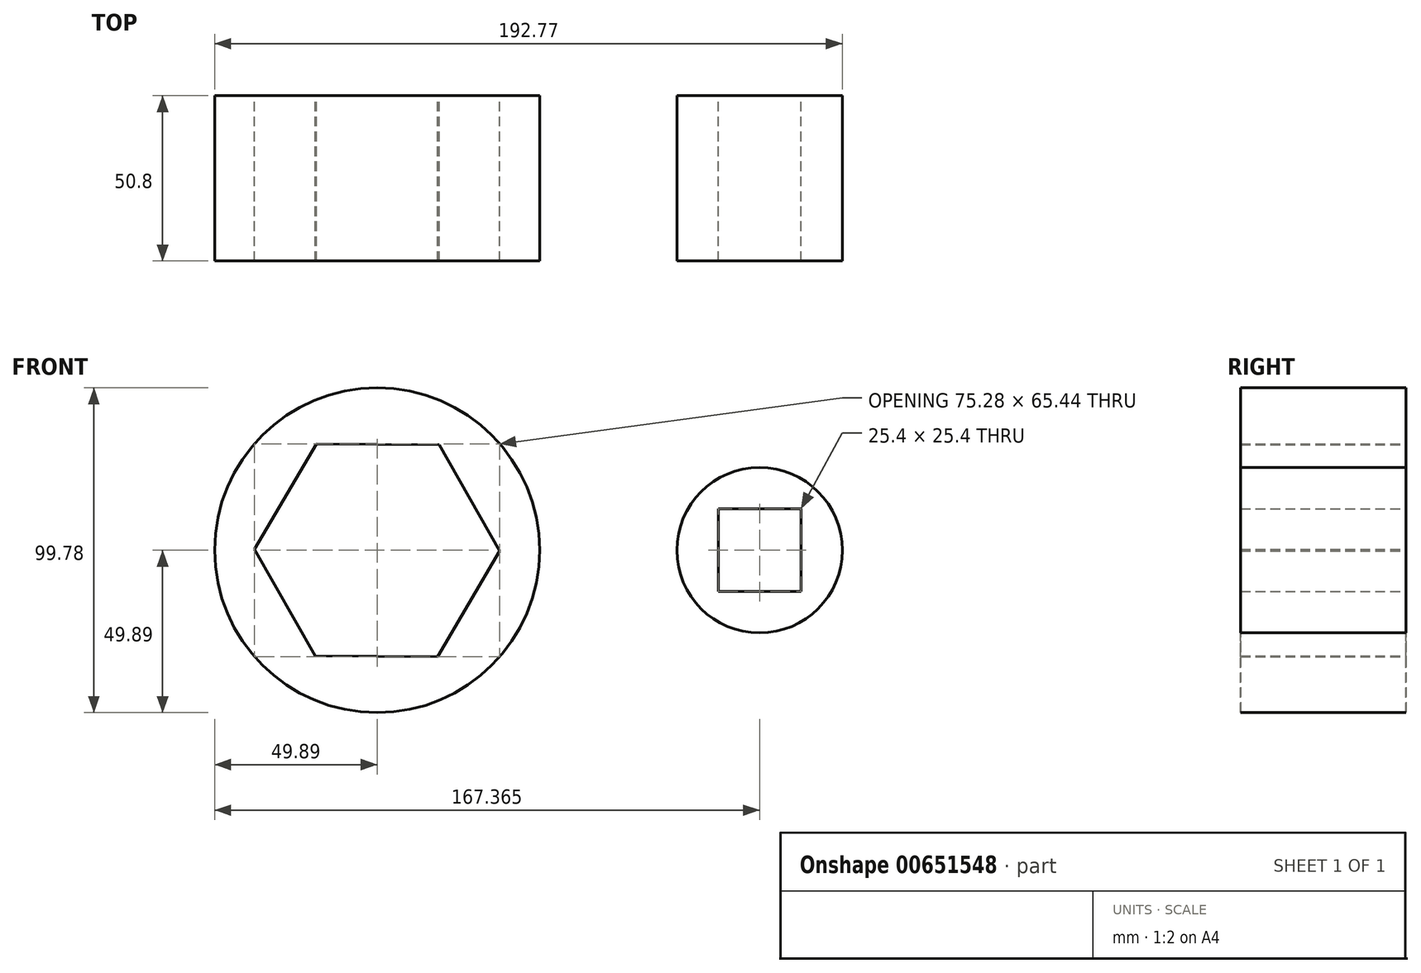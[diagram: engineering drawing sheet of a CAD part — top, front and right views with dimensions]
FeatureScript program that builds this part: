
annotation { "Feature Type Name" : "Feature", "Feature Type Description" : "" }
export const myFeature = defineFeature(function(context is Context, id is Id, definition is map)
    precondition{}
    {
        {
            var Q0;
            Q0=qCreatedBy(makeId("Front.planeOp"),FACE);
            var sketch = newSketch(context, id + "F0", { "sketchPlane" : qUnion([Q0])});
            skCircle(sketch, "E0", {"center": v(0, 0) * mm, "radius": 49.9 * mm});
            skCircle(sketch, "E1", {"center": v(117.48, 0) * mm, "radius": 25.4 * mm});
            skPoint(sketch, "E2", {"position": v(73.03, 12.7) * mm});
            skPoint(sketch, "E3", {"position": v(73.45, -12.7) * mm});
            skPoint(sketch, "E4", {"position": v(38.1, 33.02) * mm});
            skPoint(sketch, "E5", {"position": v(38.1, -33.02) * mm});
            skPoint(sketch, "E6", {"position": v(117.48, 25.4) * mm});
            skPoint(sketch, "E7", {"position": v(117.48, -25.4) * mm});
            skFitSpline(sketch, "E8", {"points": [v(38.1, 33.02) * mm, v(73.03, 12.7) * mm, v(107.2, 23.23) * mm], "startDerivative": vector(67.08, -55.18) * mm, "endDerivative": vector(71.18, 36.5) * mm});
            skFitSpline(sketch, "E9", {"points": [v(38.1, -33.02) * mm, v(73.45, -12.7) * mm, v(107.27, -23.26) * mm], "startDerivative": vector(67.83, 55.08) * mm, "endDerivative": vector(70.55, -36.59) * mm});
            skLineSegment(sketch, "E10.bottom", {"start": v(104.78, 12.7) * mm, "end": v(130.18, 12.7) * mm});
            skLineSegment(sketch, "E10.top", {"start": v(104.78, -12.7) * mm, "end": v(130.18, -12.7) * mm});
            skLineSegment(sketch, "E10.left", {"start": v(104.78, 12.7) * mm, "end": v(104.78, -12.7) * mm});
            skLineSegment(sketch, "E10.right", {"start": v(130.18, 12.7) * mm, "end": v(130.18, -12.7) * mm});
            skCircle(sketch, "E11.cCircle", {"center": v(0, 0) * mm, "radius": 37.64 * mm, "construction": true});
            skLineSegment(sketch, "E11.0", {"start": v(-18.6, 32.72) * mm, "end": v(19.04, 32.47) * mm});
            skLineSegment(sketch, "E11.1", {"start": v(19.04, 32.47) * mm, "end": v(37.64, -0.25) * mm});
            skLineSegment(sketch, "E11.2", {"start": v(37.64, -0.25) * mm, "end": v(18.6, -32.72) * mm});
            skLineSegment(sketch, "E11.3", {"start": v(18.6, -32.72) * mm, "end": v(-19.04, -32.47) * mm});
            skLineSegment(sketch, "E11.4", {"start": v(-19.04, -32.47) * mm, "end": v(-37.64, 0.25) * mm});
            skLineSegment(sketch, "E11.5", {"start": v(-37.64, 0.25) * mm, "end": v(-18.6, 32.72) * mm});
            skSolve(sketch);
        }
        {
            var Q0;
            Q0 = qSketchRegion(id + "F0", true);
            extrude(context, id + "F1", {"entities" : qUnion([Q0]), "depth" : 50.8 * mm, "offsetDistance" : 25.4 * mm});
        }
    });
